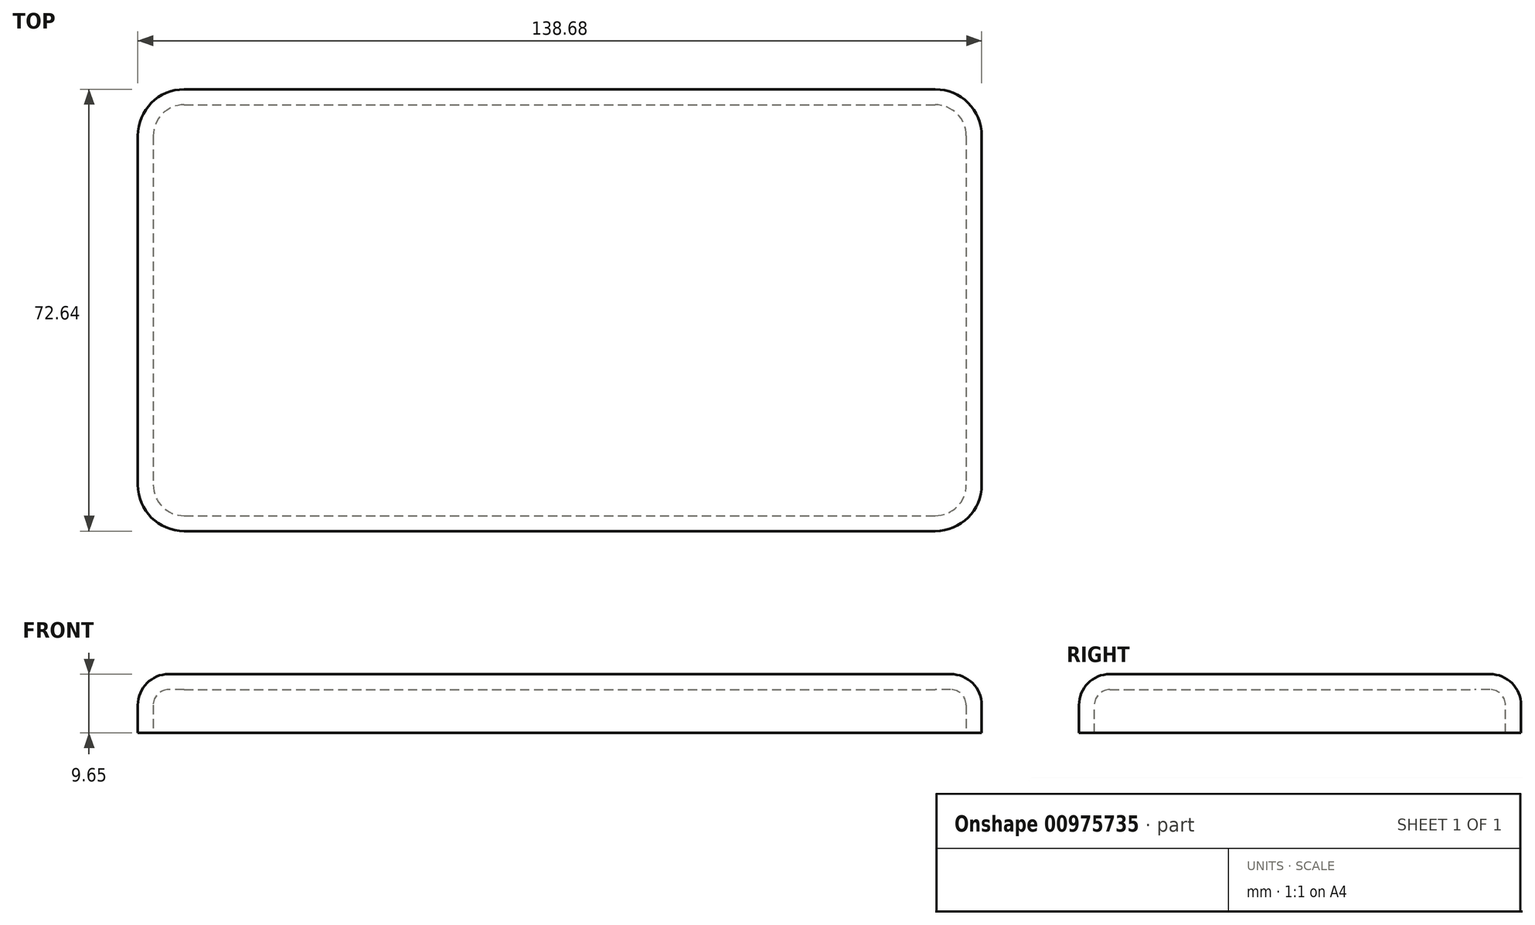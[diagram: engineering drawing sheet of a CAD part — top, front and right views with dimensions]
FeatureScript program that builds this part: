
annotation { "Feature Type Name" : "Feature", "Feature Type Description" : "" }
export const myFeature = defineFeature(function(context is Context, id is Id, definition is map)
    precondition{}
    {
        {
            var Q0;
            Q0=qCreatedBy(makeId("Top.planeOp"),FACE);
            var sketch = newSketch(context, id + "F0", { "sketchPlane" : qUnion([Q0])});
            skLineSegment(sketch, "E0.bottom", {"start": v(0, 0) * mm, "end": v(138.68, 0) * mm});
            skLineSegment(sketch, "E0.top", {"start": v(0, -72.64) * mm, "end": v(138.68, -72.64) * mm});
            skLineSegment(sketch, "E0.left", {"start": v(0, 0) * mm, "end": v(0, -72.64) * mm});
            skLineSegment(sketch, "E0.right", {"start": v(138.68, 0) * mm, "end": v(138.68, -72.64) * mm});
            skSolve(sketch);
        }
        {
            var Q0;
            Q0 = qSketchRegion(id + "F0", true);
            extrude(context, id + "F1", {"entities" : qUnion([Q0]), "depth" : 9.65 * mm, "offsetDistance" : 25.4 * mm});
        }
        {
            var Q0;
            Q0=makeQuery(id+"F1.opExtrude","SWEPT_EDGE",EDGE,{"disambiguationData":[OSD([sQuery(id+"F0.wireOp",EDGE,"E0.top"),sQuery(id+"F0.wireOp",EDGE,"E0.left")])]});
            var Q1;
            Q1=makeQuery(id+"F1.opExtrude","SWEPT_EDGE",EDGE,{"disambiguationData":[OSD([sQuery(id+"F0.wireOp",EDGE,"E0.bottom"),sQuery(id+"F0.wireOp",EDGE,"E0.left")])]});
            var Q2;
            Q2=makeQuery(id+"F1.opExtrude","SWEPT_EDGE",EDGE,{"disambiguationData":[OSD([sQuery(id+"F0.wireOp",EDGE,"E0.bottom"),sQuery(id+"F0.wireOp",EDGE,"E0.right")])]});
            var Q3;
            Q3=makeQuery(id+"F1.opExtrude","SWEPT_EDGE",EDGE,{"disambiguationData":[OSD([sQuery(id+"F0.wireOp",EDGE,"E0.top"),sQuery(id+"F0.wireOp",EDGE,"E0.right")])]});
            fillet(context, id + "F2", {"entities" : qUnion([Q0, Q1, Q2, Q3]), "radius" : 7.62 * mm, "tangentPropagation" : true, "allowEdgeOverflow" : false});
        }
        {
            var Q0;
            Q0=makeQuery(id+"F1.opExtrude","CAP_EDGE",EDGE,{"disambiguationData":[OSD([sQuery(id+"F0.wireOp",EDGE,"E0.top")])],"isStart":false});
            fillet(context, id + "F3", {"entities" : qUnion([Q0]), "radius" : 5.08 * mm, "tangentPropagation" : true, "allowEdgeOverflow" : false});
        }
        {
            var Q0;
            Q0=makeQuery(id+"F1.opExtrude","CAP_FACE",FACE,{"disambiguationData":[OSD([sQuery(id+"F0.wireOp",EDGE,"E0.bottom"),sQuery(id+"F0.wireOp",EDGE,"E0.top"),sQuery(id+"F0.wireOp",EDGE,"E0.left"),sQuery(id+"F0.wireOp",EDGE,"E0.right")])],"isStart":true});
            shell(context, id + "F4", {"entities" : qUnion([Q0]), "thickness" : 2.54 * mm});
        }
    });
